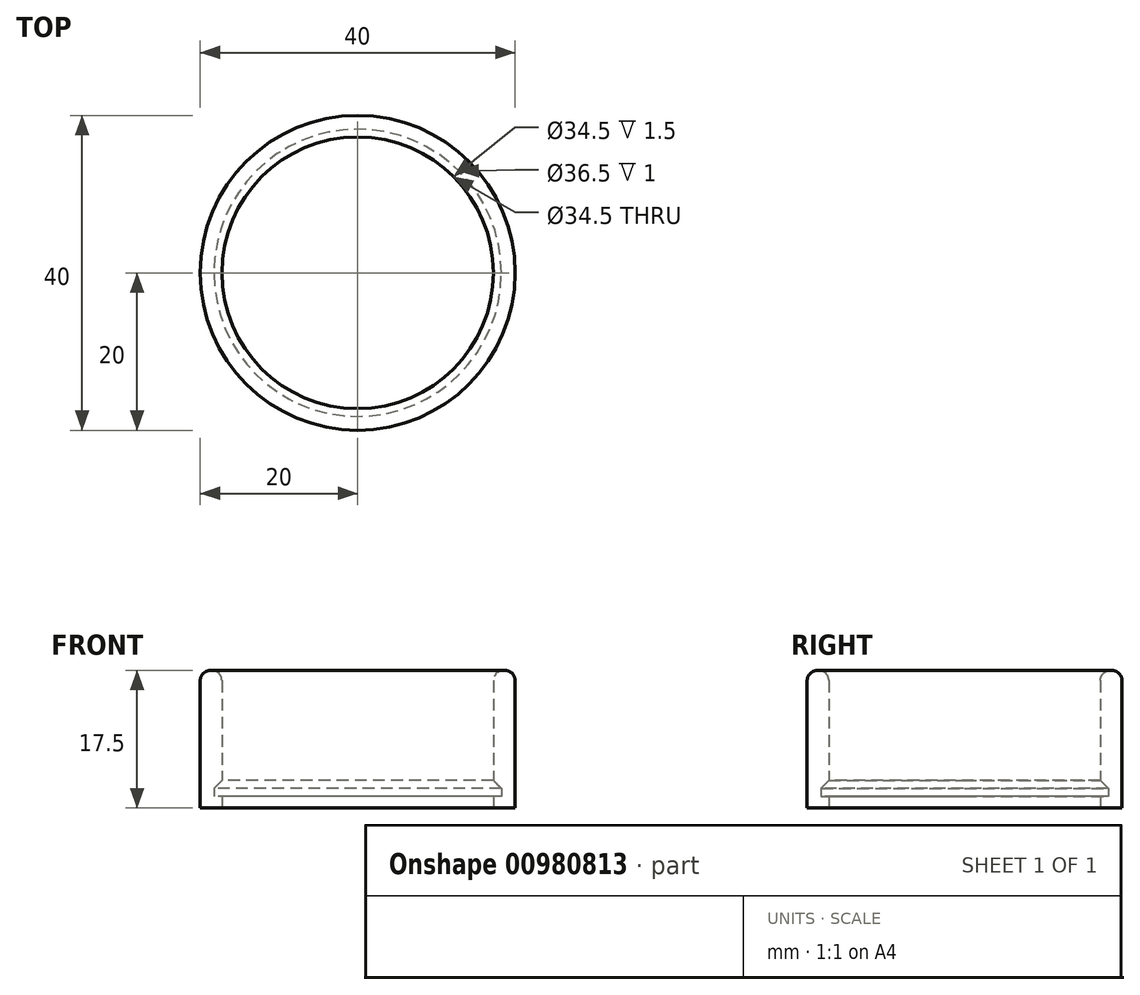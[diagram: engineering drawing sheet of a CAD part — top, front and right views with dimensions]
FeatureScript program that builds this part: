
annotation { "Feature Type Name" : "Feature", "Feature Type Description" : "" }
export const myFeature = defineFeature(function(context is Context, id is Id, definition is map)
    precondition{}
    {
        {
            var Q0;
            Q0=qCreatedBy(makeId("Top.planeOp"),FACE);
            var sketch = newSketch(context, id + "F0", { "sketchPlane" : qUnion([Q0])});
            skCircle(sketch, "E0", {"center": v(0, 0) * mm, "radius": 20 * mm});
            skCircle(sketch, "E1", {"center": v(0, 0) * mm, "radius": 17.25 * mm});
            skSolve(sketch);
        }
        {
            var Q0;
            Q0 = qSketchRegion(id + "F0", true);
            extrude(context, id + "F1", {"entities" : qUnion([Q0]), "depth" : 1.5 * mm, "offsetDistance" : 25 * mm});
        }
        {
            var Q0;
            Q0=makeQuery(id+"F1.opExtrude","CAP_FACE",FACE,{"disambiguationData":[OSD([sQuery(id+"F0.wireOp",EDGE,"E0"),sQuery(id+"F0.wireOp",EDGE,"E1")])],"isStart":false});
            var sketch = newSketch(context, id + "F2", { "sketchPlane" : qUnion([Q0])});
            skCircle(sketch, "E2.0", {"center": v(0, 0) * mm, "radius": 20 * mm});
            skCircle(sketch, "E3", {"center": v(0, 0) * mm, "radius": 18.25 * mm});
            skSolve(sketch);
        }
        {
            var Q0;
            Q0 = qSketchRegion(id + "F2", true);
            extrude(context, id + "F3", {"entities" : qUnion([Q0]), "operationType" : NewBodyOperationType.ADD, "depth" : 1 * mm, "offsetDistance" : 25 * mm});
        }
        {
            var Q0;
            Q0=makeQuery(id+"F3.opExtrude","CAP_FACE",FACE,{"disambiguationData":[OSD([sQuery(id+"F2.wireOp",EDGE,"E2.0"),sQuery(id+"F2.wireOp",EDGE,"E3")])],"isStart":false});
            var sketch = newSketch(context, id + "F4", { "sketchPlane" : qUnion([Q0])});
            skCircle(sketch, "E4.0", {"center": v(0, 0) * mm, "radius": 20 * mm});
            skCircle(sketch, "E5.0", {"center": v(0, 0) * mm, "radius": 17.25 * mm});
            skSolve(sketch);
        }
        {
            var Q0;
            Q0 = qSketchRegion(id + "F4", true);
            extrude(context, id + "F5", {"entities" : qUnion([Q0]), "operationType" : NewBodyOperationType.ADD, "depth" : 15 * mm, "offsetDistance" : 25 * mm});
        }
        {
            var Q0;
            Q0=makeQuery(id+"F5.opExtrude","CAP_EDGE",EDGE,{"disambiguationData":[OSD([sQuery(id+"F4.wireOp",EDGE,"E5.0")])],"isStart":false});
            var Q1;
            Q1=makeQuery(id+"F5.opExtrude","CAP_EDGE",EDGE,{"disambiguationData":[OSD([sQuery(id+"F4.wireOp",EDGE,"E4.0")])],"isStart":false});
            fillet(context, id + "F6", {"entities" : qUnion([Q0, Q1]), "radius" : 1.3 * mm, "tangentPropagation" : true, "allowEdgeOverflow" : false});
        }
        {
            var Q0;
            Q0=makeQuery(id+"F5.opExtrude","CAP_EDGE",EDGE,{"disambiguationData":[OSD([sQuery(id+"F4.wireOp",EDGE,"E5.0")])],"isStart":true});
            chamfer(context, id + "F7", {"entities" : qUnion([Q0]), "width" : 1 * mm, "tangentPropagation" : true});
        }
    });
